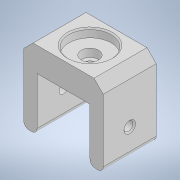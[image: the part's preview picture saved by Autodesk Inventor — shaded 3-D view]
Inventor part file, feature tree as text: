
AUTODESK INVENTOR PART (.ipt)
format: ipt  version: 2022 (Build 260153000, 153)  size: 168,448 bytes
history: native  units: mm
features: sketch x3, extrude x3, hole x2, chamfer x2, projected_geometry x2, fillet x1
ambient origin geometry x8: Origin, YZ Plane, XZ Plane, XY Plane, X Axis, Y Axis, Z Axis, Center Point
bodies: Solid1 (feature_tree)
feature tree (13):
  sketch  "Sketch1"  dims[d0=30.0mm d1=16.0mm]
  extrude  "Extrusion1"  Depth=30.0mm
  extrude  "Extrusion2"  Depth=6.0mm TaperAngle=0.0deg
  hole  "Hole1"  [1 undecoded]
  extrude  "Extrusion3"  Depth=5.0mm
  chamfer  "Chamfer1"  Distance=20.0mm
  fillet  "Fillet1"  Radius=2.0mm
  hole  "Hole2"  [1 undecoded]
  chamfer  "Chamfer2"  Distance=2.0mm Angle=45.0deg
  sketch  "Sketch2"  dims[d2=20.0mm d3=6.0mm d4=0.0mm]
  projected_geometry  "Projected Loop1"
  sketch  "Sketch3"  dims[d5=3.2mm d6=0.0mm d7=3.4mm d8=6.0mm d9=6.5mm d10=3.05mm d11=90.0deg d12=10.0mm d13=0.0mm d14=5.0mm d15=5.0mm d16=20.0mm d17=0.0mm d18=3.5mm d19=2.0mm d20=45.0deg d21=2.0mm d22=3.4mm d23=6.0mm d24=6.5mm d25=3.05mm d26=14.3117mm d27=10.0mm d28=0.0mm d29=0.5mm d30=2.0mm d31=45.0deg]
  projected_geometry  "Projected Loop2"
note: 2 required parameter values undecoded (feature->parameter linkage not recoverable at this tier; creation-order binding heuristic only, values carry confidence <= 0.55)
